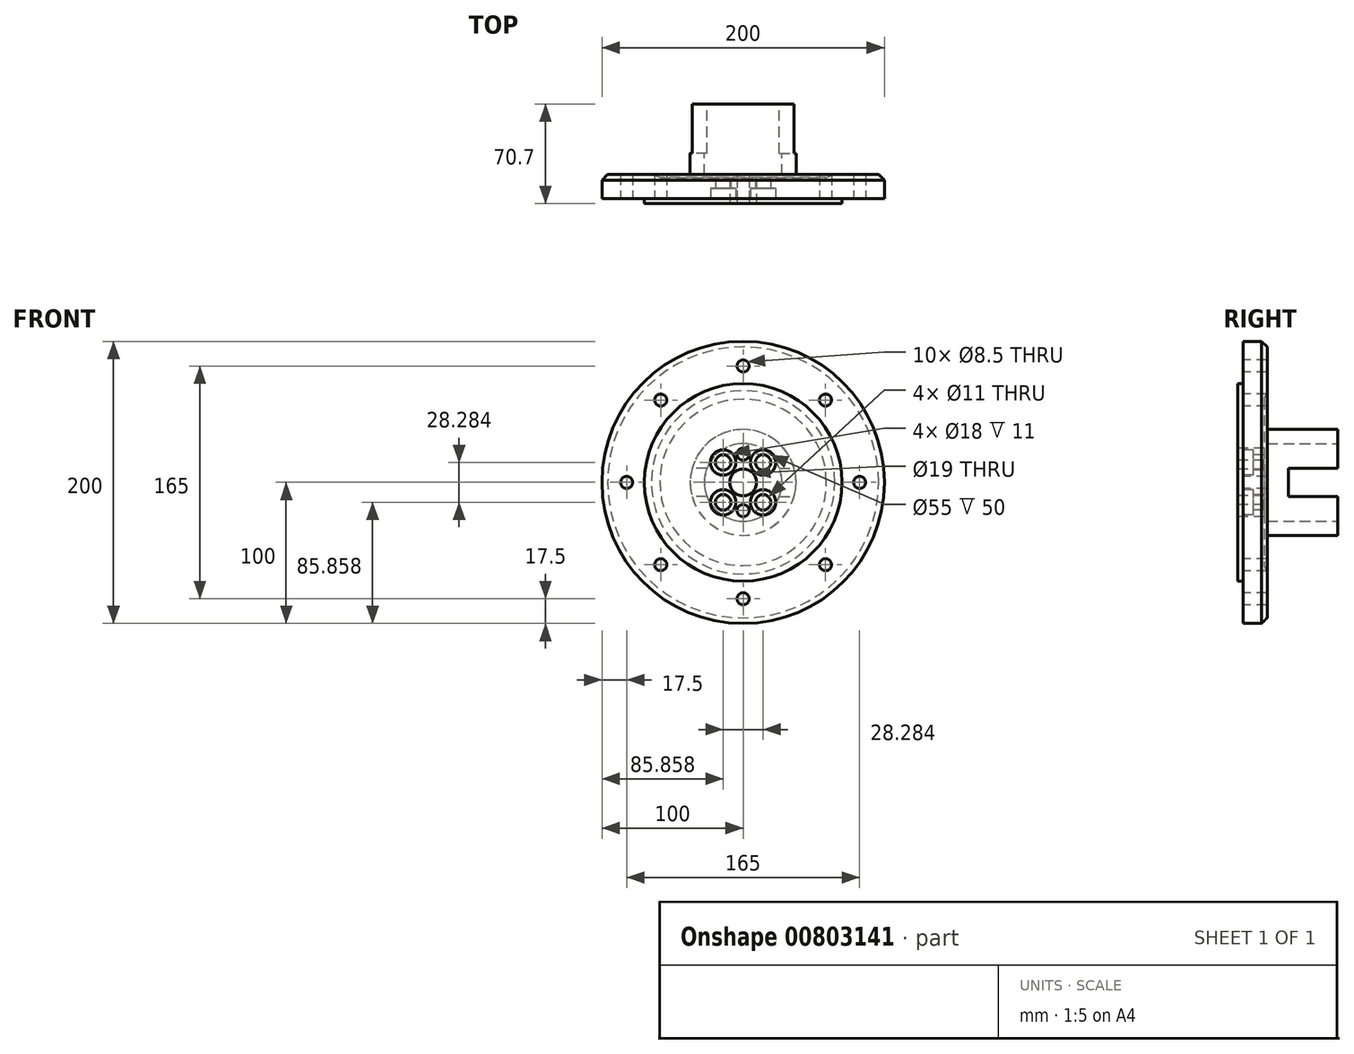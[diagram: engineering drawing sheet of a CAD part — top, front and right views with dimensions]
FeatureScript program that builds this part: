
annotation { "Feature Type Name" : "Feature", "Feature Type Description" : "" }
export const myFeature = defineFeature(function(context is Context, id is Id, definition is map)
    precondition{}
    {
        {
            var Q0;
            Q0=qCreatedBy(makeId("Front.planeOp"),FACE);
            var sketch = newSketch(context, id + "F0", { "sketchPlane" : qUnion([Q0])});
            skCircle(sketch, "E0", {"center": v(0, 0) * mm, "radius": 100 * mm});
            skCircle(sketch, "E1", {"center": v(0, 0) * mm, "radius": 70 * mm});
            skSolve(sketch);
        }
        {
            var Q0;
            Q0=makeQuery(id+"F0.imprint","IMPRINT",FACE,{"disambiguationData":[TD([[makeQuery(id+"F0.imprint","IMPRINT",EDGE,{"derivedFrom":sQuery(id+"F0.wireOp",EDGE,"E1")}),1.0]])]});
            extrude(context, id + "F1", {"entities" : qUnion([Q0]), "depth" : 3.7 * mm, "offsetDistance" : 25 * mm});
        }
        {
            var Q0;
            Q0=makeQuery(id+"F0.imprint","IMPRINT",FACE,{"disambiguationData":[TD([[makeQuery(id+"F0.imprint","IMPRINT",EDGE,{"derivedFrom":sQuery(id+"F0.wireOp",EDGE,"E0")}),1.0]])]});
            var Q1;
            Q1=makeQuery(id+"F0.imprint","IMPRINT",FACE,{"disambiguationData":[TD([[makeQuery(id+"F0.imprint","IMPRINT",EDGE,{"derivedFrom":sQuery(id+"F0.wireOp",EDGE,"E1")}),1.0]])]});
            extrude(context, id + "F2", {"entities" : qUnion([Q0, Q1]), "operationType" : NewBodyOperationType.ADD, "oppositeDirection" : true, "depth" : 17 * mm, "offsetDistance" : 25 * mm});
        }
        {
            var Q0;
            Q0=makeQuery(id+"F2.opExtrude","CAP_FACE",FACE,{"disambiguationData":[OSD([sQuery(id+"F0.wireOp",EDGE,"E0")])],"isStart":false});
            cPlane(context, id + "F3", {"entities" : qUnion([Q0]), "cplaneType" : CPlaneType.OFFSET, "offset" : 0 * mm, "width" : 150 * mm, "height" : 150 * mm});
        }
        {
            var Q0;
            Q0=qCreatedBy(id+"F3.planeOp",FACE);
            var sketch = newSketch(context, id + "F4", { "sketchPlane" : qUnion([Q0])});
            skCircle(sketch, "E2", {"center": v(0, 0) * mm, "radius": 37.5 * mm});
            skSolve(sketch);
        }
        {
            var Q0;
            Q0=makeQuery(id+"F4.imprint","IMPRINT",FACE,{"disambiguationData":[TD([[makeQuery(id+"F4.imprint","IMPRINT",EDGE,{"derivedFrom":sQuery(id+"F4.wireOp",EDGE,"E2")}),1.0]])]});
            extrude(context, id + "F5", {"entities" : qUnion([Q0]), "operationType" : NewBodyOperationType.ADD, "depth" : 50 * mm, "offsetDistance" : 25 * mm});
        }
        {
            var Q0;
            Q0=qCreatedBy(id+"F3.planeOp",FACE);
            var sketch = newSketch(context, id + "F6", { "sketchPlane" : qUnion([Q0])});
            skCircle(sketch, "E3", {"center": v(0, 0) * mm, "radius": 65 * mm});
            skSolve(sketch);
        }
        {
            var Q0;
            Q0=qCreatedBy(id+"F3.planeOp",FACE);
            cPlane(context, id + "F7", {"entities" : qUnion([Q0]), "cplaneType" : CPlaneType.OFFSET, "offset" : 2 * mm, "oppositeDirection" : true, "width" : 150 * mm, "height" : 150 * mm});
        }
        {
            var Q0;
            Q0=qCreatedBy(id+"F7.planeOp",FACE);
            var sketch = newSketch(context, id + "F8", { "sketchPlane" : qUnion([Q0])});
            skCircle(sketch, "E4", {"center": v(0, 0) * mm, "radius": 59 * mm});
            skSolve(sketch);
        }
        {
            var Q1;
            Q1 = qSketchRegion(id + "F8", true);
            var Q2;
            Q2=makeQuery(id+"F6.imprint","IMPRINT",FACE,{"disambiguationData":[TD([[makeQuery(id+"F6.imprint","IMPRINT",EDGE,{"derivedFrom":sQuery(id+"F6.wireOp",EDGE,"E3")}),1.0]])]});
            loft(context, id + "F9", {"operationType" : NewBodyOperationType.REMOVE, "sheetProfilesArray" : [{ "sheetProfileEntities" : qUnion([Q1]) }, { "sheetProfileEntities" : qUnion([Q2]) }]});
        }
        {
            var Q0;
            Q0=makeQuery(id+"F2.opExtrude","CAP_EDGE",EDGE,{"disambiguationData":[OSD([sQuery(id+"F0.wireOp",EDGE,"E0")])],"isStart":false});
            chamfer(context, id + "F10", {"entities" : qUnion([Q0]), "width" : 4 * mm, "tangentPropagation" : true});
        }
        {
            var Q0;
            Q0=qCreatedBy(id+"F3.planeOp",FACE);
            cPlane(context, id + "F11", {"entities" : qUnion([Q0]), "cplaneType" : CPlaneType.OFFSET, "offset" : 50 * mm, "width" : 150 * mm, "height" : 150 * mm});
        }
        {
            var Q0;
            Q0=qCreatedBy(id+"F11.planeOp",FACE);
            var sketch = newSketch(context, id + "F12", { "sketchPlane" : qUnion([Q0])});
            skCircle(sketch, "E5", {"center": v(0, 0) * mm, "radius": 27.5 * mm});
            skSolve(sketch);
        }
        {
            var Q0;
            Q0=makeQuery(id+"F12.imprint","IMPRINT",FACE,{"disambiguationData":[TD([[makeQuery(id+"F12.imprint","IMPRINT",EDGE,{"derivedFrom":sQuery(id+"F12.wireOp",EDGE,"E5")}),1.0]])]});
            extrude(context, id + "F13", {"entities" : qUnion([Q0]), "operationType" : NewBodyOperationType.REMOVE, "oppositeDirection" : true, "depth" : 51 * mm, "offsetDistance" : 25 * mm});
        }
        {
            var Q0;
            Q0=makeQuery(id+"F5.opExtrude","CAP_FACE",FACE,{"disambiguationData":[OSD([sQuery(id+"F4.wireOp",EDGE,"E2")])],"isStart":false});
            var sketch = newSketch(context, id + "F14", { "sketchPlane" : qUnion([Q0])});
            skLineSegment(sketch, "E6", {"start": v(-25.62, 10) * mm, "end": v(-36.14, 10) * mm});
            skLineSegment(sketch, "E7", {"start": v(-25.62, -10) * mm, "end": v(-36.14, -10) * mm});
            skLineSegment(sketch, "E8", {"start": v(25.62, -10) * mm, "end": v(36.14, -10) * mm});
            skLineSegment(sketch, "E9", {"start": v(25.62, 10) * mm, "end": v(36.14, 10) * mm});
            skSolve(sketch);
        }
        {
            var Q0;
            {var subQ0=sQuery(id+"F14.wireOp",EDGE,"E6");Q0=makeQuery(id+"F14.imprint","IMPRINT",FACE,{"disambiguationData":[TD([[makeQuery(id+"F14.imprint","IMPRINT",EDGE,{"derivedFrom":subQ0}),1.0]])]});}
            var Q1;
            {var subQ0=sQuery(id+"F14.wireOp",EDGE,"E8");Q1=makeQuery(id+"F14.imprint","IMPRINT",FACE,{"disambiguationData":[TD([[makeQuery(id+"F14.imprint","IMPRINT",EDGE,{"derivedFrom":subQ0}),1.0]])]});}
            extrude(context, id + "F15", {"entities" : qUnion([Q0, Q1]), "operationType" : NewBodyOperationType.REMOVE, "oppositeDirection" : true, "depth" : 35 * mm, "offsetDistance" : 25 * mm});
        }
        {
            var Q0;
            Q0=makeQuery(id+"F1.opExtrude","CAP_FACE",FACE,{"disambiguationData":[OSD([sQuery(id+"F0.wireOp",EDGE,"E1")])],"isStart":false});
            var sketch = newSketch(context, id + "F16", { "sketchPlane" : qUnion([Q0])});
            skCircle(sketch, "E10", {"center": v(0, 0) * mm, "radius": 9.5 * mm});
            skSolve(sketch);
        }
        {
            var Q0;
            Q0=makeQuery(id+"F16.imprint","IMPRINT",FACE,{"disambiguationData":[TD([[makeQuery(id+"F16.imprint","IMPRINT",EDGE,{"derivedFrom":sQuery(id+"F16.wireOp",EDGE,"E10")}),1.0]])]});
            extrude(context, id + "F17", {"entities" : qUnion([Q0]), "operationType" : NewBodyOperationType.REMOVE, "oppositeDirection" : true, "depth" : 20.7 * mm, "offsetDistance" : 25 * mm});
        }
        {
            var Q0;
            Q0=makeQuery(id+"F1.opExtrude","CAP_FACE",FACE,{"disambiguationData":[OSD([sQuery(id+"F0.wireOp",EDGE,"E1")])],"isStart":false});
            var sketch = newSketch(context, id + "F18", { "sketchPlane" : qUnion([Q0])});
            skCircle(sketch, "E11", {"center": v(14.14, 14.14) * mm, "radius": 5.5 * mm});
            skCircle(sketch, "E12", {"center": v(-14.14, 14.14) * mm, "radius": 5.5 * mm});
            skCircle(sketch, "E13", {"center": v(-14.14, -14.14) * mm, "radius": 5.5 * mm});
            skCircle(sketch, "E14", {"center": v(14.14, -14.14) * mm, "radius": 5.5 * mm});
            skCircle(sketch, "E15", {"center": v(-14.14, 14.14) * mm, "radius": 9 * mm});
            skCircle(sketch, "E16", {"center": v(14.14, 14.14) * mm, "radius": 9 * mm});
            skCircle(sketch, "E17", {"center": v(14.14, -14.14) * mm, "radius": 9 * mm});
            skCircle(sketch, "E18", {"center": v(-14.14, -14.14) * mm, "radius": 9 * mm});
            skCircle(sketch, "E19", {"center": v(0, 20) * mm, "radius": 4.25 * mm});
            skCircle(sketch, "E20", {"center": v(0, -20) * mm, "radius": 4.25 * mm});
            skSolve(sketch);
        }
        {
            var Q0;
            Q0=makeQuery(id+"F18.imprint","IMPRINT",FACE,{"disambiguationData":[TD([[makeQuery(id+"F18.imprint","IMPRINT",EDGE,{"derivedFrom":sQuery(id+"F18.wireOp",EDGE,"E12")}),1.0]])]});
            var Q1;
            Q1=makeQuery(id+"F18.imprint","IMPRINT",FACE,{"disambiguationData":[TD([[makeQuery(id+"F18.imprint","IMPRINT",EDGE,{"derivedFrom":sQuery(id+"F18.wireOp",EDGE,"E11")}),1.0]])]});
            var Q2;
            Q2=makeQuery(id+"F18.imprint","IMPRINT",FACE,{"disambiguationData":[TD([[makeQuery(id+"F18.imprint","IMPRINT",EDGE,{"derivedFrom":sQuery(id+"F18.wireOp",EDGE,"E14")}),1.0]])]});
            var Q3;
            Q3=makeQuery(id+"F18.imprint","IMPRINT",FACE,{"disambiguationData":[TD([[makeQuery(id+"F18.imprint","IMPRINT",EDGE,{"derivedFrom":sQuery(id+"F18.wireOp",EDGE,"E13")}),1.0]])]});
            var Q4;
            Q4=makeQuery(id+"F18.imprint","IMPRINT",FACE,{"disambiguationData":[TD([[makeQuery(id+"F18.imprint","IMPRINT",EDGE,{"derivedFrom":sQuery(id+"F18.wireOp",EDGE,"E20")}),1.0]])]});
            var Q5;
            Q5=makeQuery(id+"F18.imprint","IMPRINT",FACE,{"disambiguationData":[TD([[makeQuery(id+"F18.imprint","IMPRINT",EDGE,{"derivedFrom":sQuery(id+"F18.wireOp",EDGE,"E19")}),1.0]])]});
            extrude(context, id + "F19", {"entities" : qUnion([Q0, Q1, Q2, Q3, Q4, Q5]), "operationType" : NewBodyOperationType.REMOVE, "oppositeDirection" : true, "depth" : 20.7 * mm, "offsetDistance" : 25 * mm});
        }
        {
            var Q0;
            Q0=makeQuery(id+"F18.imprint","IMPRINT",FACE,{"disambiguationData":[TD([[makeQuery(id+"F18.imprint","IMPRINT",EDGE,{"derivedFrom":sQuery(id+"F18.wireOp",EDGE,"E12")}),-1.0]])]});
            var Q1;
            Q1=makeQuery(id+"F18.imprint","IMPRINT",FACE,{"disambiguationData":[TD([[makeQuery(id+"F18.imprint","IMPRINT",EDGE,{"derivedFrom":sQuery(id+"F18.wireOp",EDGE,"E11")}),-1.0]])]});
            var Q2;
            Q2=makeQuery(id+"F18.imprint","IMPRINT",FACE,{"disambiguationData":[TD([[makeQuery(id+"F18.imprint","IMPRINT",EDGE,{"derivedFrom":sQuery(id+"F18.wireOp",EDGE,"E14")}),-1.0]])]});
            var Q3;
            Q3=makeQuery(id+"F18.imprint","IMPRINT",FACE,{"disambiguationData":[TD([[makeQuery(id+"F18.imprint","IMPRINT",EDGE,{"derivedFrom":sQuery(id+"F18.wireOp",EDGE,"E13")}),-1.0]])]});
            extrude(context, id + "F20", {"entities" : qUnion([Q0, Q1, Q2, Q3]), "operationType" : NewBodyOperationType.REMOVE, "oppositeDirection" : true, "depth" : 11 * mm, "offsetDistance" : 25 * mm});
        }
        {
            var Q0;
            Q0=makeQuery(id+"F2.opExtrude","CAP_FACE",FACE,{"disambiguationData":[OSD([sQuery(id+"F0.wireOp",EDGE,"E0")])],"isStart":true});
            var sketch = newSketch(context, id + "F21", { "sketchPlane" : qUnion([Q0])});
            skLineSegment(sketch, "E21", {"start": v(0, -100) * mm, "end": v(0, 0) * mm, "construction": true});
            skLineSegment(sketch, "E22", {"start": v(0, 0) * mm, "end": v(0, 100) * mm, "construction": true});
            skLineSegment(sketch, "E23", {"start": v(70.71, -70.71) * mm, "end": v(0, 0) * mm, "construction": true});
            skLineSegment(sketch, "E24", {"start": v(0, 0) * mm, "end": v(-70.71, 70.71) * mm, "construction": true});
            skLineSegment(sketch, "E25", {"start": v(0, 0) * mm, "end": v(70.71, 70.71) * mm, "construction": true});
            skLineSegment(sketch, "E26", {"start": v(0, 0) * mm, "end": v(100, 0) * mm, "construction": true});
            skLineSegment(sketch, "E27", {"start": v(0, 0) * mm, "end": v(-70.71, -70.71) * mm, "construction": true});
            skLineSegment(sketch, "E28", {"start": v(0, 0) * mm, "end": v(-100, 0) * mm, "construction": true});
            skCircle(sketch, "E29", {"center": v(0, 82.5) * mm, "radius": 4.25 * mm});
            skCircle(sketch, "E30", {"center": v(58.34, 58.34) * mm, "radius": 4.25 * mm});
            skCircle(sketch, "E31", {"center": v(82.5, 0) * mm, "radius": 4.25 * mm});
            skCircle(sketch, "E32", {"center": v(58.34, -58.34) * mm, "radius": 4.25 * mm});
            skCircle(sketch, "E33", {"center": v(0, -82.5) * mm, "radius": 4.25 * mm});
            skCircle(sketch, "E34", {"center": v(-58.34, -58.34) * mm, "radius": 4.25 * mm});
            skCircle(sketch, "E35", {"center": v(-82.5, 0) * mm, "radius": 4.25 * mm});
            skCircle(sketch, "E36", {"center": v(-58.34, 58.34) * mm, "radius": 4.25 * mm});
            skSolve(sketch);
        }
        {
            var Q0;
            Q0=makeQuery(id+"F21.imprint","IMPRINT",FACE,{"disambiguationData":[TD([[makeQuery(id+"F21.imprint","IMPRINT",EDGE,{"derivedFrom":sQuery(id+"F21.wireOp",EDGE,"E36")}),1.0]])]});
            var Q1;
            Q1=makeQuery(id+"F21.imprint","IMPRINT",FACE,{"disambiguationData":[TD([[makeQuery(id+"F21.imprint","IMPRINT",EDGE,{"derivedFrom":sQuery(id+"F21.wireOp",EDGE,"E29")}),1.0]])]});
            var Q2;
            Q2=makeQuery(id+"F21.imprint","IMPRINT",FACE,{"disambiguationData":[TD([[makeQuery(id+"F21.imprint","IMPRINT",EDGE,{"derivedFrom":sQuery(id+"F21.wireOp",EDGE,"E30")}),1.0]])]});
            var Q3;
            Q3=makeQuery(id+"F21.imprint","IMPRINT",FACE,{"disambiguationData":[TD([[makeQuery(id+"F21.imprint","IMPRINT",EDGE,{"derivedFrom":sQuery(id+"F21.wireOp",EDGE,"E31")}),1.0]])]});
            var Q4;
            Q4=makeQuery(id+"F21.imprint","IMPRINT",FACE,{"disambiguationData":[TD([[makeQuery(id+"F21.imprint","IMPRINT",EDGE,{"derivedFrom":sQuery(id+"F21.wireOp",EDGE,"E32")}),1.0]])]});
            var Q5;
            Q5=makeQuery(id+"F21.imprint","IMPRINT",FACE,{"disambiguationData":[TD([[makeQuery(id+"F21.imprint","IMPRINT",EDGE,{"derivedFrom":sQuery(id+"F21.wireOp",EDGE,"E33")}),1.0]])]});
            var Q6;
            Q6=makeQuery(id+"F21.imprint","IMPRINT",FACE,{"disambiguationData":[TD([[makeQuery(id+"F21.imprint","IMPRINT",EDGE,{"derivedFrom":sQuery(id+"F21.wireOp",EDGE,"E34")}),1.0]])]});
            var Q7;
            Q7=makeQuery(id+"F21.imprint","IMPRINT",FACE,{"disambiguationData":[TD([[makeQuery(id+"F21.imprint","IMPRINT",EDGE,{"derivedFrom":sQuery(id+"F21.wireOp",EDGE,"E35")}),1.0]])]});
            extrude(context, id + "F22", {"entities" : qUnion([Q0, Q1, Q2, Q3, Q4, Q5, Q6, Q7]), "operationType" : NewBodyOperationType.REMOVE, "oppositeDirection" : true, "depth" : 17 * mm, "offsetDistance" : 25 * mm});
        }
    });
